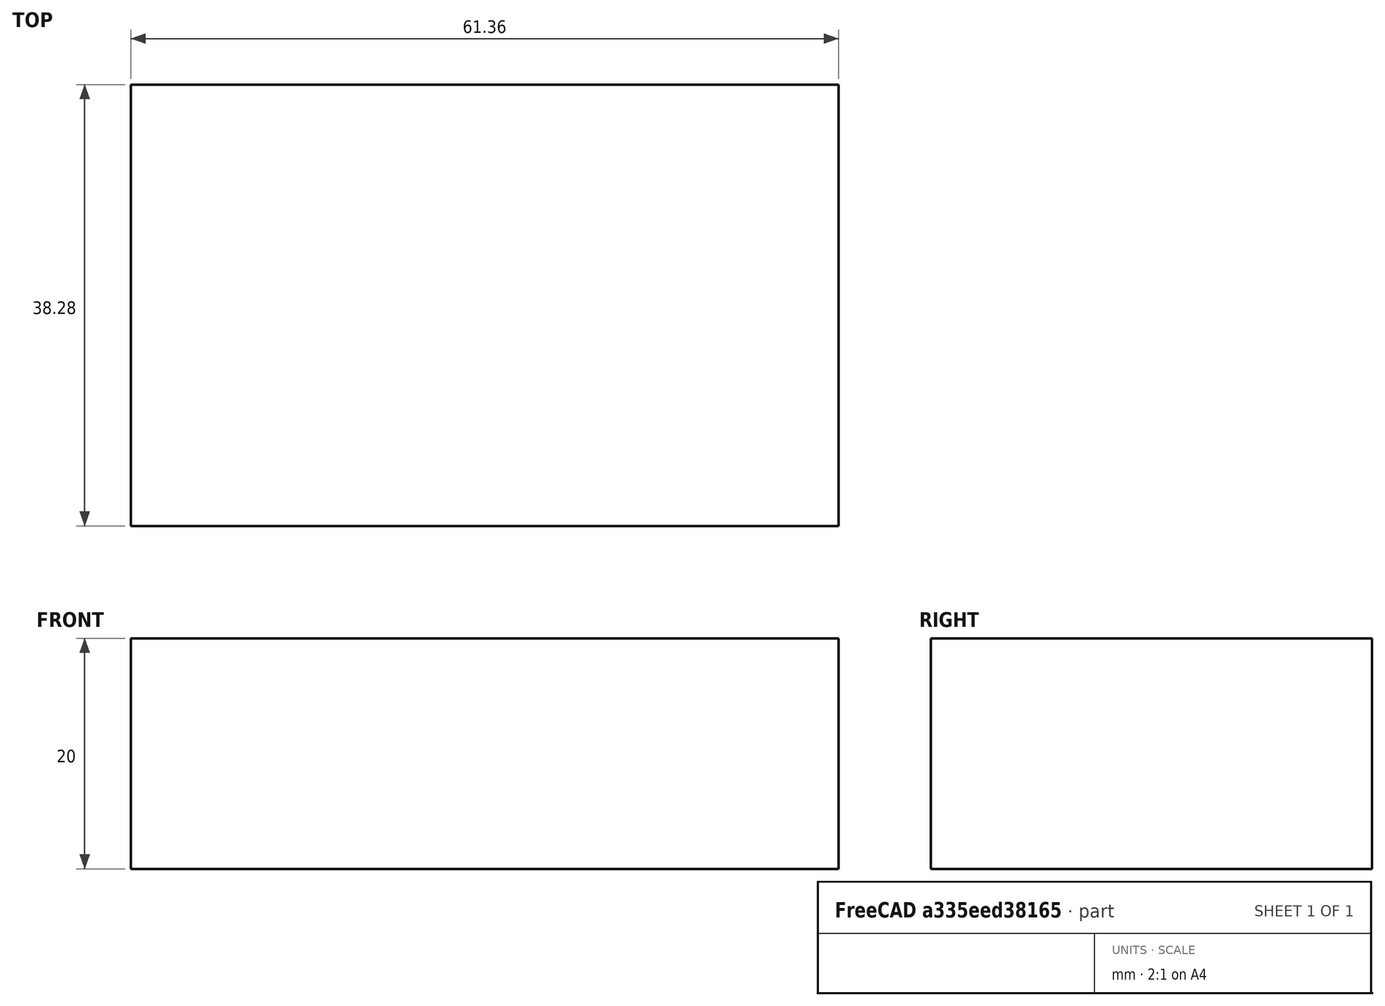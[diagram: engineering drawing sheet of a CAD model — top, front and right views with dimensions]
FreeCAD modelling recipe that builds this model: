
FCSTD DOCUMENT  (FreeCAD 0.19R21300 +2313 (Git))
Label: test1
License: All rights reserved
LicenseURL: http://en.wikipedia.org/wiki/All_rights_reserved
objects: App::FeaturePython×2, Part::FeaturePython×2, Sketcher::SketchObject×1, PartDesign::Pad×1, PartDesign::Body×1
note: 6 computed .brp shape members not serialized (recipe doc carries the construction recipe); baked Part::Feature solids carry a one-line shape summary decoded from their .brp

FEATURE [App::FeaturePython] Constraints  # WARN: FeaturePython — macro-defined, semantics opaque (R4)
  _Version = 1
FEATURE [App::FeaturePython] Elements  # WARN: FeaturePython — macro-defined, semantics opaque (R4)
FEATURE [Sketcher::SketchObject] Sketch
  MapMode = 5
  Support = -> [XY_Plane]
  sketch-geometry (4):
    g0: LineSegment StartX=-65.147 StartY=39.6232 StartZ=0 EndX=-3.78956 EndY=39.6232 EndZ=0
    g1: LineSegment StartX=-3.78956 StartY=39.6232 StartZ=0 EndX=-3.78956 EndY=1.33749 EndZ=0
    g2: LineSegment StartX=-3.78956 StartY=1.33749 StartZ=0 EndX=-65.147 EndY=1.33749 EndZ=0
    g3: LineSegment StartX=-65.147 StartY=1.33749 StartZ=0 EndX=-65.147 EndY=39.6232 EndZ=0
  constraints (8):
    c: Coincident(g0,g1)
    c: Coincident(g1,g2)
    c: Coincident(g2,g3)
    c: Coincident(g3,g0)
    c: Horizontal(g0)
    c: Horizontal(g2)
    c: Vertical(g1)
    c: Vertical(g3)
FEATURE [PartDesign::Pad] Pad
  ClaimChildren = false
  Length = 20
  Length2 = 100
  Profile = -> Sketch
  Suppress = false
  Type = 0
FEATURE [PartDesign::Body] Body
  ExportMode = 0
  Group = -> [Sketch,Pad]
  Origin = -> Origin
  Tip = -> Pad
  _ExportChildren = -> [Pad]
  _GroupVersion = 1
FEATURE [Part::FeaturePython] Parts  # WARN: FeaturePython — macro-defined, semantics opaque (R4)
  Group = -> [Body]
  GroupMode = 0
FEATURE [Part::FeaturePython] Assembly  label="test1"  # WARN: FeaturePython — macro-defined, semantics opaque (R4)
  AutoRelax = true
  BuildShape = 0
  Freeze = false
  Group = -> [Constraints,Elements,Parts]
  Verbose = false
  _SolverType = 1
  _Version = 1
